# Revit family: NBS_HarlequinFloors_WoodFltngFlrSystms_HarlequinFlexity
name_source: partatom
category: Furniture
units: mm (PartAtom-declared; Revit-internal decimal feet)

## family parameters
Always vertical = Yes
Cut with Voids When Loaded = No
Room Calculation Point = No
Shared = No
Work Plane-Based = No

## types (1)
- HarlequinFlexity
    AssetType = Movable
    BIMObjectName = NBS_HarlequinFloors_WoodFloatingFloorSystems_HarlequinFlexity
    CalcFloorDamperSpacing = 350 mm  [stored 1.14829 ft]
    Category = Ss_30_20_95_95:Wood floating floor systems
    CategoryOfUse = A4
    DurationUnit = year
    DynamicLoading = >1500 N (69 kg/cm²)
    ExpansionGapLength = 10 mm  [stored 0.0328084 ft]
    FloorDamperMaterial = NBS_Concept
    FloorDamperSpacing = 350 mm  [stored 1.14829 ft]
    FloorDamperThickness = 19 mm  [stored 0.062336 ft]
    FloorStructureMaterial = NBS_Concept
    FloorStructureThickness = 18 mm  [stored 0.0590551 ft]
    FloorSurfaceMaterial = NBS_Concept
    FloorSurfaceThickness = 2 mm  [stored 0.00656168 ft]
    FlooringBoardType = Plywood
    IfcExportAs = IfcCoveringType
    IfcExportType = FLOORING
    InstallationMethod = Tongue and groove
    IsPermanment = No
    IsPortable = Yes
    Load = 1126 kN (229 kg/cm²)
    ManufacturerName = Harlequin Floors (British Harlequin plc)
    ManufacturerURL = www.harlequinfloors.com
    Material = Plywood
    ModelReference = HarlequinFlexity
    NBSCertification = www.nationalbimlibrary.com/cert/vzefzhb3
    Name = WoodFloatingFloorSystems_HarlequinFlexity_HarlequinFloors
    NominalHeight = 39 mm  [stored 0.127953 ft]
    NominalLength = 2250 mm
    NominalWidth = 1125 mm
    NumberFloorDamperSets = 6
    ReactionToFire = Class 3 BS 476-7 (Bfls1 with Standfast)
    Shape = Rectangle
    ShockAbsorption = 67%
    SubfloorPreparationLayer = Smooth, flat, hard surface
    ThermalInsulation = 0.658 W/m²K
    ThermalResistance = 1.52 m²K/W
    TopLayer = Engineered board with a hardwood layer
    Underlay = Harlequin engineered board
    Uniclass2015Code = Ss_30_20_95_95
    Uniclass2015Title = Wood floating floor systems
    Uniclass2015Version = Systems v1.22
    Version = 3
    WarrantyDescription = Ten year
    WarrantyDurationUnit = year
    WearLayer = Harlequin performance vinyl
    Weight = 11.85 kg/m²

note: [stored X ft] marks values corroborated as IEEE doubles in the binary element streams (Revit-internal decimal feet)

## geometry (parser evidence)
native form markers: Sweep x2
no freeform markers — native parametric forms only
